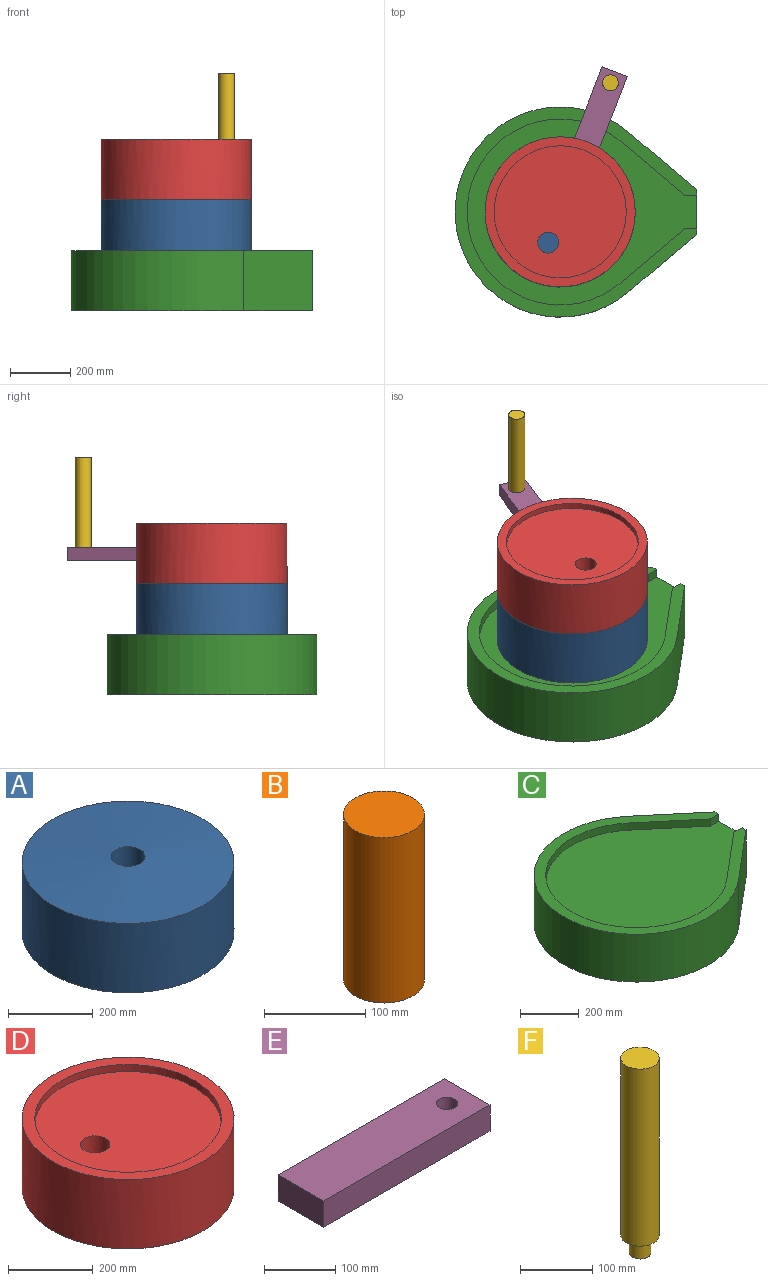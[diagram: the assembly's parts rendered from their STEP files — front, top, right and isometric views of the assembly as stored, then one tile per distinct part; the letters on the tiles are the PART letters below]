
ASSEMBLY  parts=6 mates=5
PART A: 5 faces, bbox 500x500x216.8 mm
  f0: cone r=250mm half-angle=85.4deg, axis (0,0,-1), area 191934.2mm2, adj f1,f3
  f1: cylinder r=250mm len=500mm, axis (0,0,-1), area 314159.3mm2, adj f0,f2
  f2: plane 500x500mm, normal (0,0,-1), area 196349.5mm2, adj f1
  f3: cylinder r=40mm len=116.8mm, axis (0,0,-1), area 29355mm2, adj f0,f4
  f4: plane 80x80mm, normal (0,0,1), area 5026.5mm2, adj f3
PART B: 3 faces, bbox 80x80x200 mm
  f0: cylinder r=40mm len=200mm, axis (0,0,-1), area 50265.5mm2, adj f1,f2
  f1: plane 80x80mm, normal (0,0,1), area 5026.5mm2, adj f0
  f2: plane 80x80mm, normal (0,0,-1), area 5026.5mm2, adj f0
PART C: 12 faces, bbox 804.8x700x200 mm
  f0: plane 200x150mm, normal (1,0,0), area 26618.2mm2, adj f1,f3,f4,f5,f6,f10,f11
  f1: plane 804.84x700mm, normal (0,0,1), area 83915.9mm2, adj f0,f2,f3,f4,f6,f7,f8,f9
  f2: cylinder r=350mm len=700mm, axis (0,0,-1), area 317735.9mm2, adj f1,f3,f4,f5
  f3: plane 229.7x200mm, normal (0.64,-0.77,0), area 60000mm2, adj f0,f1,f2,f5
  f4: plane 229.7x200mm, normal (0.64,0.77,0), area 60000mm2, adj f0,f1,f2,f5
  f5: plane 804.84x700mm, normal (0,0,-1), area 417131.5mm2, adj f0,f2,f3,f4
  f6: plane 40x30mm, normal (0,-1,0), area 1200mm2, adj f0,f1,f7,f11
  f7: plane 215.43x180.99mm, normal (-0.64,-0.77,0), area 8440.9mm2, adj f1,f6,f8,f11
  f8: cylinder r=310mm len=620mm, axis (0,0,1), area 42213.5mm2, adj f1,f7,f9,f11
  f9: plane 215.43x180.99mm, normal (-0.64,0.77,0), area 8440.9mm2, adj f1,f8,f10,f11
  f10: plane 40x30mm, normal (0,1,0), area 1200mm2, adj f0,f1,f9,f11
  f11: plane 764.84x620mm, normal (0,0,1), area 333215.6mm2, adj f0,f6,f7,f8,f9,f10
PART D: 13 faces, bbox 500x500x200 mm
  f0: cylinder r=250mm len=500mm, axis (0,0,-1), area 310087.1mm2, adj f1,f2,f8,f9,f10,f11
  f1: cone r=250mm half-angle=85.4deg, axis (0,0,-1), area 188073.4mm2, adj f0,f3,f7
  f2: plane 500x500mm, normal (0,0,1), area 44296.5mm2, adj f0,f5
  f3: cylinder r=40mm len=83.2mm, axis (0,0,-1), area 20910.4mm2, adj f1,f4
  f4: plane 80x80mm, normal (0,0,-1), area 5026.5mm2, adj f3
  f5: cylinder r=220mm len=440mm, axis (0,0,1), area 27646mm2, adj f2,f6
  f6: plane 440x440mm, normal (0,0,1), area 148204.6mm2, adj f5,f7
  f7: cylinder r=35mm len=171.6mm, axis (0,0,1), area 37170.4mm2, adj f1,f6
  f8: plane 90x79.17mm, normal (0,0,-1), area 7002.7mm2, adj f0,f9,f11,f12
  f9: plane 75.08x45mm, normal (0,1,0), area 3378.7mm2, adj f0,f8,f10,f12
  f10: plane 90x79.17mm, normal (0,0,1), area 7002.7mm2, adj f0,f9,f11,f12
  f11: plane 75.08x45mm, normal (0,-1,0), area 3378.7mm2, adj f0,f8,f10,f12
  f12: plane 90x45mm, normal (1,0,0), area 4050mm2, adj f8,f9,f10,f11
PART E: 8 faces, bbox 330x90x45 mm
  f0: plane 330x90mm, normal (0,0,1), area 28993.1mm2, adj f1,f3,f4,f5,f6
  f1: plane 330x45mm, normal (0,-1,0), area 14850mm2, adj f0,f2,f4,f5
  f2: plane 330x90mm, normal (0,0,-1), area 29700mm2, adj f1,f3,f4,f5
  f3: plane 330x45mm, normal (0,1,0), area 14850mm2, adj f0,f2,f4,f5
  f4: plane 90x45mm, normal (-1,0,0), area 4050mm2, adj f0,f1,f2,f3
  f5: plane 90x45mm, normal (1,0,0), area 4050mm2, adj f0,f1,f2,f3
  f6: cylinder r=15mm len=30mm, axis (0,0,1), area 2827.4mm2, adj f0,f7
  f7: plane 30x30mm, normal (0,0,1), area 706.9mm2, adj f6
PART F: 5 faces, bbox 53.1x53.1x330 mm
  f0: cylinder r=15mm len=30mm, axis (0,0,1), area 2827.4mm2, adj f1,f4
  f1: plane 30x30mm, normal (0,0,-1), area 706.9mm2, adj f0
  f2: cylinder r=26.57mm len=300mm, axis (0,0,-1), area 50083.7mm2, adj f3,f4
  f3: plane 53.14x53.14mm, normal (0,0,1), area 2217.9mm2, adj f2
  f4: plane 53.14x53.14mm, normal (0,0,-1), area 1511mm2, adj f0,f2
PLACE A at identity
PLACE B at identity
PLACE C at identity fixed
PLACE D rot(axis=(0,0,1),68.7deg) t=(0,0,0)mm
PLACE E rot(axis=(0,0,1),68.7deg) t=(0,0,0)mm
PLACE F rot(axis=(0,0,1),68.7deg) t=(0,0,0)mm
MATE revolute D.f3 <-> B.f0  axis (0,0,-1) through (0,0,470)mm
MATE fastened A.f1 <-> C.f8  axis (0,0,-1) through (0,0,170)mm
MATE fastened F.f0 <-> E.f6  axis (0,0,-1) through (167.32,429.39,460)mm
MATE fastened E.f4 <-> D.f12  axis (-0.36,-0.93,0) through (62.03,159.18,467.5)mm
MATE fastened A.f3 <-> B.f0  axis (0,0,1) through (0,0,270)mm
